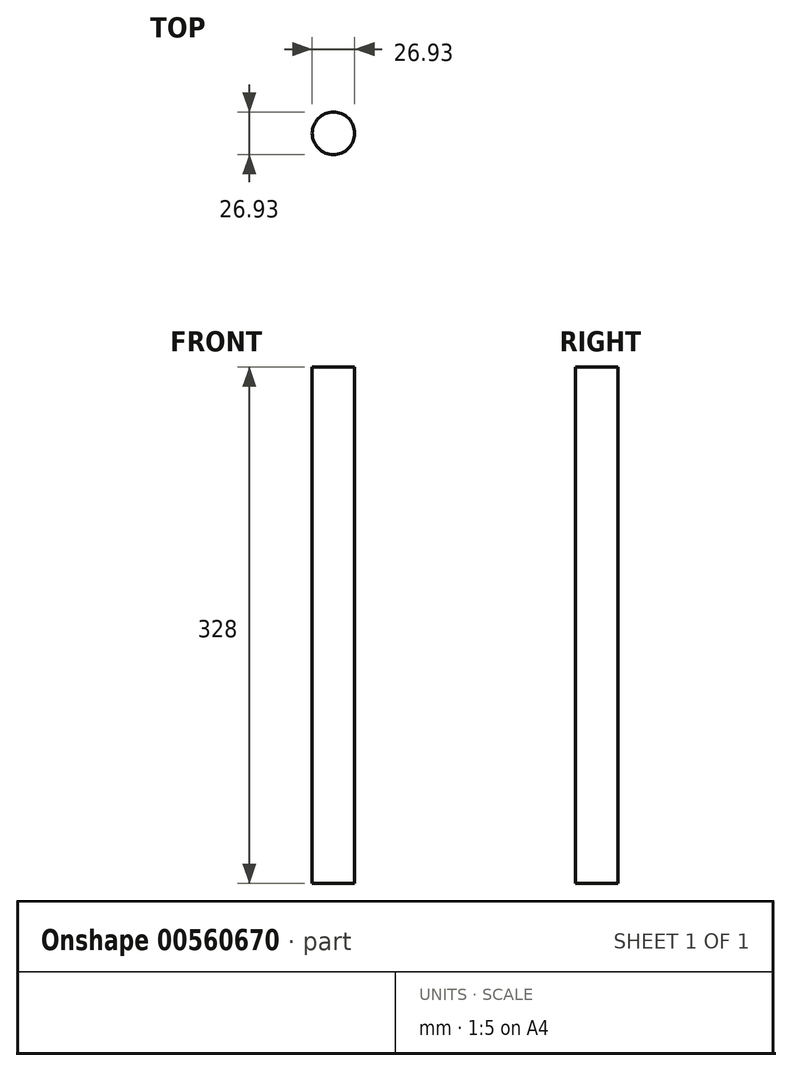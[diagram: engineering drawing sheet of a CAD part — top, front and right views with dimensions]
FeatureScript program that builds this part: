
annotation { "Feature Type Name" : "Feature", "Feature Type Description" : "" }
export const myFeature = defineFeature(function(context is Context, id is Id, definition is map)
    precondition{}
    {
        {
            var Q0;
            Q0=qCreatedBy(makeId("Top.planeOp"),FACE);
            var sketch = newSketch(context, id + "F0", { "sketchPlane" : qUnion([Q0])});
            skCircle(sketch, "E0", {"center": v(4.38, -12.74) * mm, "radius": 13.47 * mm});
            skPoint(sketch, "E0.first.point", {"position": v(0, 0) * mm});
            skPoint(sketch, "E0.second.point", {"position": v(-3.41, -23.72) * mm});
            skPoint(sketch, "E0.third.point", {"position": v(8.77, 0) * mm});
            skSolve(sketch);
        }
        {
            var Q0;
            Q0=makeQuery(id+"F0.imprint","IMPRINT",FACE,{"disambiguationData":[TD([[makeQuery(id+"F0.imprint","IMPRINT",EDGE,{"derivedFrom":sQuery(id+"F0.wireOp",EDGE,"E0")}),1.0]])]});
            extrude(context, id + "F1", {"entities" : qUnion([Q0]), "oppositeDirection" : true, "depth" : 328 * mm, "offsetDistance" : 25 * mm});
        }
    });
